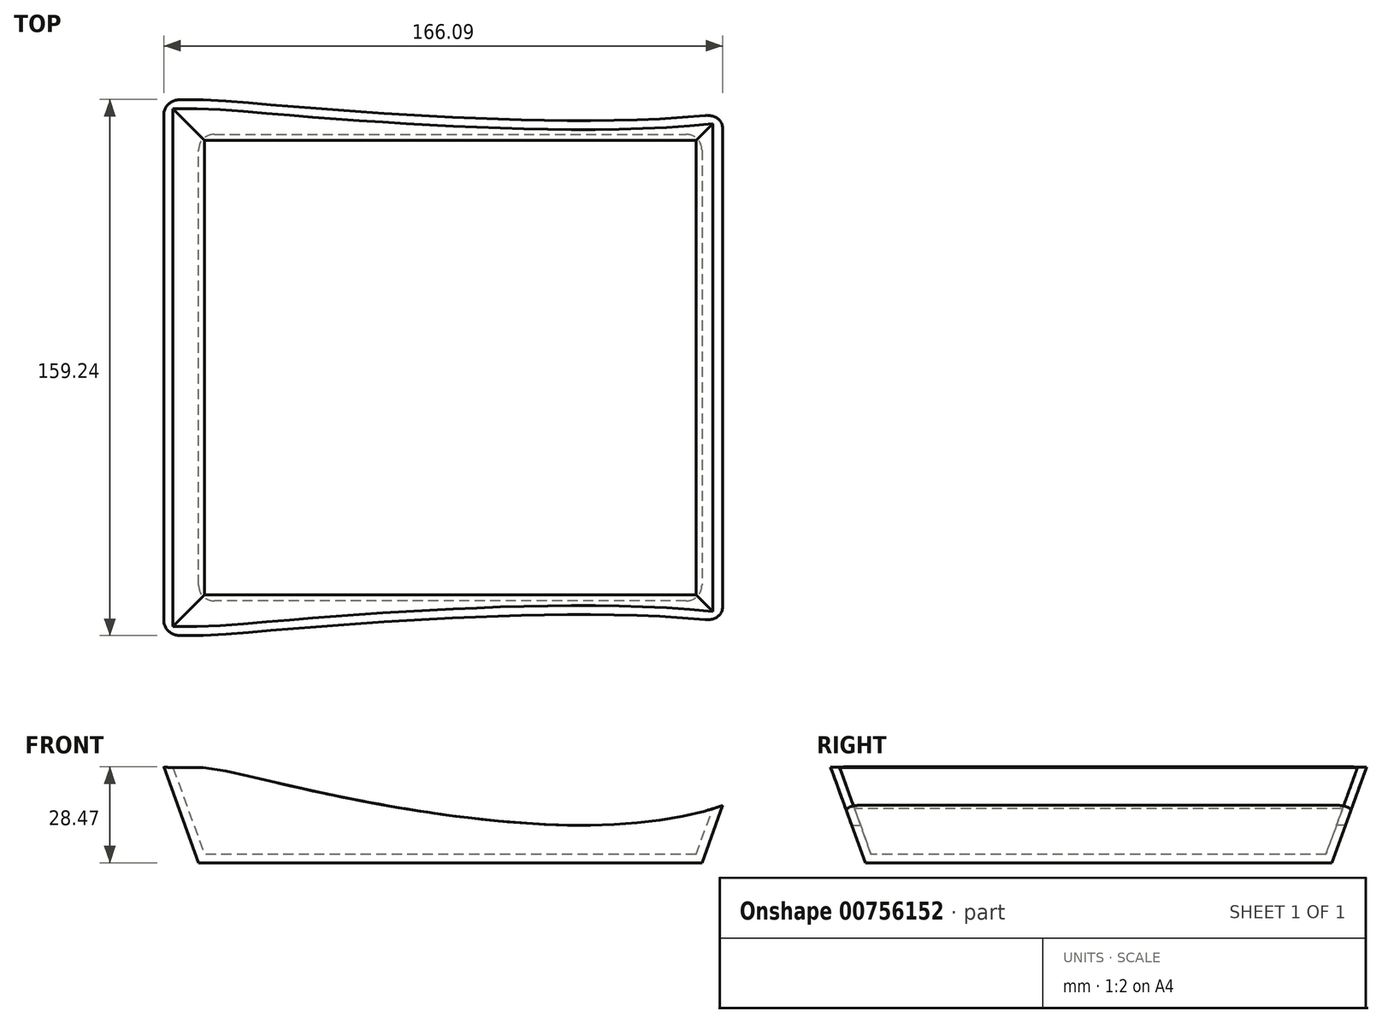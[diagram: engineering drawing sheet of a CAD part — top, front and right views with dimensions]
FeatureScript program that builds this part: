
annotation { "Feature Type Name" : "Feature", "Feature Type Description" : "" }
export const myFeature = defineFeature(function(context is Context, id is Id, definition is map)
    precondition{}
    {
        {
            var Q0;
            Q0=qCreatedBy(makeId("Top.planeOp"),FACE);
            var sketch = newSketch(context, id + "F0", { "sketchPlane" : qUnion([Q0])});
            skLineSegment(sketch, "E0.bottom", {"start": v(74.76, -69.3) * mm, "end": v(-74.76, -69.3) * mm});
            skLineSegment(sketch, "E0.top", {"start": v(74.76, 69.3) * mm, "end": v(-74.76, 69.3) * mm});
            skLineSegment(sketch, "E0.left", {"start": v(74.76, -69.3) * mm, "end": v(74.76, 69.3) * mm});
            skLineSegment(sketch, "E0.right", {"start": v(-74.76, -69.3) * mm, "end": v(-74.76, 69.3) * mm});
            skPoint(sketch, "E0.middle", {"position": v(0, 0) * mm});
            skSolve(sketch);
        }
        {
            var Q0;
            Q0=makeQuery(id+"F0.imprint","IMPRINT",FACE,{"disambiguationData":[TD([[makeQuery(id+"F0.imprint","IMPRINT",EDGE,{"derivedFrom":sQuery(id+"F0.wireOp",EDGE,"E0.bottom")}),-1.0]])]});
            extrude(context, id + "F1", {"entities" : qUnion([Q0]), "depth" : 50 * mm, "offsetDistance" : 25 * mm, "hasDraft" : true, "draftAngle" : 20 * degree});
        }
        {
            var Q0;
            Q0=makeQuery(id+"F1.opExtrude","CAP_FACE",FACE,{"disambiguationData":[OSD([sQuery(id+"F0.wireOp",EDGE,"E0.bottom"),sQuery(id+"F0.wireOp",EDGE,"E0.top"),sQuery(id+"F0.wireOp",EDGE,"E0.left"),sQuery(id+"F0.wireOp",EDGE,"E0.right")])],"isStart":false});
            shell(context, id + "F2", {"entities" : qUnion([Q0]), "thickness" : 2.5 * mm});
        }
        {
            var Q0;
            Q0=makeQuery(id+"F1.opExtrude","SWEPT_EDGE",EDGE,{"disambiguationData":[OSD([sQuery(id+"F0.wireOp",EDGE,"E0.bottom"),sQuery(id+"F0.wireOp",EDGE,"E0.left")])]});
            var Q1;
            Q1=makeQuery(id+"F1.opExtrude","SWEPT_EDGE",EDGE,{"disambiguationData":[OSD([sQuery(id+"F0.wireOp",EDGE,"E0.top"),sQuery(id+"F0.wireOp",EDGE,"E0.left")])]});
            var Q2;
            Q2=makeQuery(id+"F1.opExtrude","SWEPT_EDGE",EDGE,{"disambiguationData":[OSD([sQuery(id+"F0.wireOp",EDGE,"E0.top"),sQuery(id+"F0.wireOp",EDGE,"E0.right")])]});
            var Q3;
            Q3=makeQuery(id+"F1.opExtrude","SWEPT_EDGE",EDGE,{"disambiguationData":[OSD([sQuery(id+"F0.wireOp",EDGE,"E0.bottom"),sQuery(id+"F0.wireOp",EDGE,"E0.right")])]});
            fillet(context, id + "F3", {"entities" : qUnion([Q0, Q1, Q2, Q3]), "radius" : 5 * mm, "tangentPropagation" : true, "allowEdgeOverflow" : false});
        }
        {
            var Q0;
            Q0=qCreatedBy(makeId("Front.planeOp"),FACE);
            var sketch = newSketch(context, id + "F4", { "sketchPlane" : qUnion([Q0])});
            skFitSpline(sketch, "E1", {"points": [v(-104.6, 68.7) * mm, v(-102.07, 48.52) * mm, v(-88.99, 29.76) * mm, v(-76.26, 28.36) * mm, v(-51.63, 23.78) * mm, v(77.63, 15.96) * mm, v(128.68, 56.68) * mm, v(128.7, 66.43) * mm, v(-104.6, 68.7) * mm]});
            skSolve(sketch);
        }
        {
            var Q0;
            Q0=makeQuery(id+"F4.imprint","IMPRINT",FACE,{"disambiguationData":[TD([[makeQuery(id+"F4.imprint","IMPRINT",EDGE,{"derivedFrom":sQuery(id+"F4.wireOp",EDGE,"E1")}),1.0]])]});
            extrude(context, id + "F5", {"entities" : qUnion([Q0]), "operationType" : NewBodyOperationType.REMOVE, "oppositeDirection" : true, "depth" : 141 * mm, "offsetDistance" : 25 * mm, "hasSecondDirection" : true, "secondDirectionOppositeDirection" : false, "secondDirectionDepth" : 150 * mm});
        }
    });
